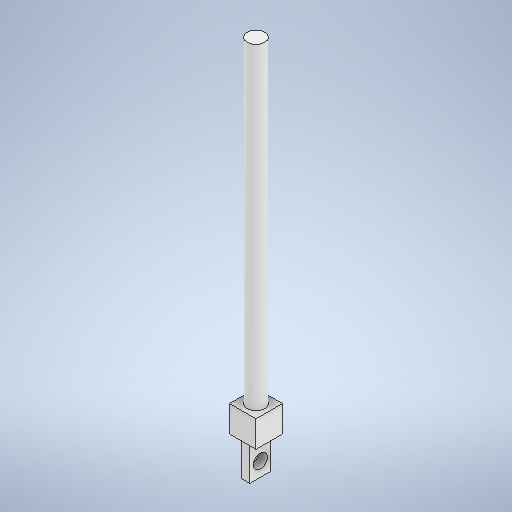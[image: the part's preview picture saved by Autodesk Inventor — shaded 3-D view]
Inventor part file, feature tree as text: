
AUTODESK INVENTOR PART (.ipt)
format: ipt  version: 2025.3 (Build 293356000, 356)  size: 276,480 bytes
history: native  units: mm
features: extrude x4, sketch x4, other x1
ambient origin geometry x8: Origin, YZ Plane, XZ Plane, XY Plane, X Axis, Y Axis, Z Axis, Center Point
bodies: Body1 (feature_tree)
feature tree (9):
  other  "pendulum"
  extrude  "Extrusión2"  Depth=180.0mm TaperAngle=0.0deg
  extrude  "Extrusión3"  Depth=15.0mm
  extrude  "Extrusión4"  Depth=5.0mm
  extrude  "Extrusión5"  Depth=20.0mm TaperAngle=0.0deg
  sketch  "Boceto3"  dims[d21=10.0mm d22=180.0mm d23=0.0mm]
  sketch  "Boceto4"  dims[d24=15.0mm d25=15.0mm]
  sketch  "Boceto5"  dims[d26=15.0mm d27=0.0mm d28=5.0mm]
  sketch  "Boceto6"  dims[d29=12.0mm d30=20.0mm d31=0.0mm d32=8.0mm d33=8.0mm d34=20.0mm d35=0.0mm d5=0.5mm d6=0.872665mm d7=0.5mm d8=0.872665mm d9=0.0mm d10=0.0mm d11=0.0mm d12=0.0mm d36=0.0mm d37=0.0mm d38=0.0mm d39=0.0mm]
